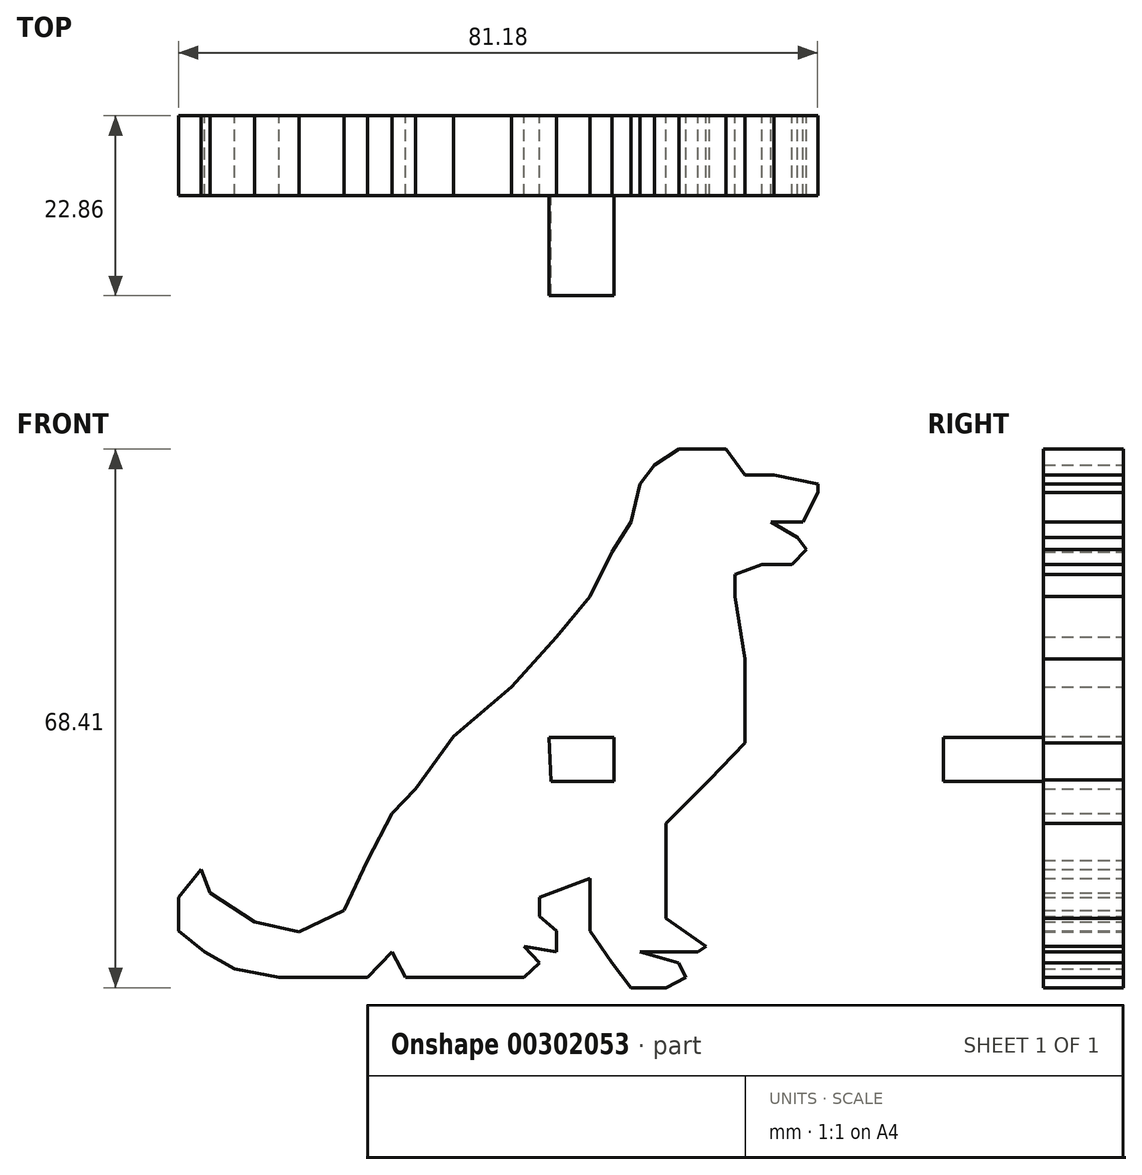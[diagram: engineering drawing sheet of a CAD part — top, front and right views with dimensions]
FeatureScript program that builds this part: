
annotation { "Feature Type Name" : "Feature", "Feature Type Description" : "" }
export const myFeature = defineFeature(function(context is Context, id is Id, definition is map)
    precondition{}
    {
        {
            var Q0;
            Q0=qCreatedBy(makeId("Front.planeOp"),FACE);
            var sketch = newSketch(context, id + "F0", { "sketchPlane" : qUnion([Q0])});
            skLineSegment(sketch, "E0", {"start": v(-46.88, 88.84) * mm, "end": v(-48.72, 86.43) * mm});
            skLineSegment(sketch, "E1", {"start": v(-48.72, 86.43) * mm, "end": v(-49.86, 81.6) * mm});
            skLineSegment(sketch, "E2", {"start": v(-49.86, 81.6) * mm, "end": v(-52.27, 77.77) * mm});
            skLineSegment(sketch, "E3", {"start": v(-52.27, 77.77) * mm, "end": v(-55.1, 72.1) * mm});
            skLineSegment(sketch, "E4", {"start": v(-55.1, 72.1) * mm, "end": v(-59.37, 66.99) * mm});
            skLineSegment(sketch, "E5", {"start": v(-59.37, 66.99) * mm, "end": v(-65.04, 60.6) * mm});
            skLineSegment(sketch, "E6", {"start": v(-65.04, 60.6) * mm, "end": v(-72.42, 54.35) * mm});
            skLineSegment(sketch, "E7", {"start": v(-72.42, 54.35) * mm, "end": v(-77.25, 47.68) * mm});
            skLineSegment(sketch, "E8", {"start": v(-77.25, 47.68) * mm, "end": v(-80.23, 44.56) * mm});
            skLineSegment(sketch, "E9", {"start": v(-80.23, 44.56) * mm, "end": v(-83.35, 38.6) * mm});
            skLineSegment(sketch, "E10", {"start": v(-83.35, 38.6) * mm, "end": v(-86.33, 32.21) * mm});
            skLineSegment(sketch, "E11", {"start": v(-86.33, 32.21) * mm, "end": v(-92, 29.52) * mm});
            skLineSegment(sketch, "E12", {"start": v(-92, 29.52) * mm, "end": v(-97.69, 30.8) * mm});
            skLineSegment(sketch, "E13", {"start": v(-97.69, 30.8) * mm, "end": v(-103.36, 34.48) * mm});
            skLineSegment(sketch, "E14", {"start": v(-103.36, 34.48) * mm, "end": v(-104.5, 37.47) * mm});
            skLineSegment(sketch, "E15", {"start": v(-104.5, 37.47) * mm, "end": v(-107.34, 33.92) * mm});
            skLineSegment(sketch, "E16", {"start": v(-107.34, 33.92) * mm, "end": v(-107.34, 29.66) * mm});
            skLineSegment(sketch, "E17", {"start": v(-107.34, 29.66) * mm, "end": v(-104.07, 26.96) * mm});
            skLineSegment(sketch, "E18", {"start": v(-104.07, 26.96) * mm, "end": v(-100.24, 24.83) * mm});
            skLineSegment(sketch, "E19", {"start": v(-100.24, 24.83) * mm, "end": v(-94.56, 23.7) * mm});
            skLineSegment(sketch, "E20", {"start": v(-94.56, 23.7) * mm, "end": v(-88.6, 23.7) * mm});
            skLineSegment(sketch, "E21", {"start": v(-88.6, 23.7) * mm, "end": v(-83.35, 23.7) * mm});
            skLineSegment(sketch, "E22", {"start": v(-83.35, 23.7) * mm, "end": v(-80.23, 26.96) * mm});
            skLineSegment(sketch, "E23", {"start": v(-80.23, 26.96) * mm, "end": v(-78.53, 23.7) * mm});
            skLineSegment(sketch, "E24", {"start": v(-78.53, 23.7) * mm, "end": v(-70.15, 23.7) * mm});
            skLineSegment(sketch, "E25", {"start": v(-70.15, 23.7) * mm, "end": v(-63.48, 23.7) * mm});
            skLineSegment(sketch, "E26", {"start": v(-63.48, 23.7) * mm, "end": v(-61.5, 25.54) * mm});
            skLineSegment(sketch, "E27", {"start": v(-61.5, 25.54) * mm, "end": v(-63.48, 27.68) * mm});
            skLineSegment(sketch, "E28", {"start": v(-63.48, 27.68) * mm, "end": v(-59.37, 26.96) * mm});
            skLineSegment(sketch, "E29", {"start": v(-59.37, 26.96) * mm, "end": v(-59.37, 29.66) * mm});
            skLineSegment(sketch, "E30", {"start": v(-59.37, 29.66) * mm, "end": v(-61.5, 31.5) * mm});
            skLineSegment(sketch, "E31", {"start": v(-61.5, 31.5) * mm, "end": v(-61.5, 33.92) * mm});
            skLineSegment(sketch, "E32", {"start": v(-61.5, 33.92) * mm, "end": v(-55.1, 36.33) * mm});
            skLineSegment(sketch, "E33", {"start": v(-55.1, 36.33) * mm, "end": v(-55.1, 29.66) * mm});
            skLineSegment(sketch, "E34", {"start": v(-55.1, 29.66) * mm, "end": v(-52.27, 25.54) * mm});
            skLineSegment(sketch, "E35", {"start": v(-52.27, 25.54) * mm, "end": v(-49.86, 22.42) * mm});
            skLineSegment(sketch, "E36", {"start": v(-49.86, 22.42) * mm, "end": v(-45.46, 22.42) * mm});
            skLineSegment(sketch, "E37", {"start": v(-45.46, 22.42) * mm, "end": v(-42.9, 23.7) * mm});
            skLineSegment(sketch, "E38", {"start": v(-42.9, 23.7) * mm, "end": v(-43.83, 25.54) * mm});
            skLineSegment(sketch, "E39", {"start": v(-43.83, 25.54) * mm, "end": v(-48.72, 26.96) * mm});
            skLineSegment(sketch, "E40", {"start": v(-48.72, 26.96) * mm, "end": v(-41.34, 26.96) * mm});
            skLineSegment(sketch, "E41", {"start": v(-41.34, 26.96) * mm, "end": v(-40.35, 27.68) * mm});
            skLineSegment(sketch, "E42", {"start": v(-40.35, 27.68) * mm, "end": v(-45.46, 31.22) * mm});
            skLineSegment(sketch, "E43", {"start": v(-45.46, 31.22) * mm, "end": v(-45.46, 36.33) * mm});
            skLineSegment(sketch, "E44", {"start": v(-45.46, 36.33) * mm, "end": v(-45.46, 43.28) * mm});
            skLineSegment(sketch, "E45", {"start": v(-45.46, 43.28) * mm, "end": v(-39.92, 48.82) * mm});
            skLineSegment(sketch, "E46", {"start": v(-39.92, 48.82) * mm, "end": v(-35.38, 53.5) * mm});
            skLineSegment(sketch, "E47", {"start": v(-35.38, 53.5) * mm, "end": v(-35.38, 58.61) * mm});
            skLineSegment(sketch, "E48", {"start": v(-35.38, 58.61) * mm, "end": v(-35.38, 64.15) * mm});
            skLineSegment(sketch, "E49", {"start": v(-35.38, 64.15) * mm, "end": v(-36.66, 72.1) * mm});
            skLineSegment(sketch, "E50", {"start": v(-36.66, 72.1) * mm, "end": v(-36.66, 74.93) * mm});
            skLineSegment(sketch, "E51", {"start": v(-36.66, 74.93) * mm, "end": v(-33.25, 76.21) * mm});
            skLineSegment(sketch, "E52", {"start": v(-33.25, 76.21) * mm, "end": v(-29.42, 76.21) * mm});
            skLineSegment(sketch, "E53", {"start": v(-29.42, 76.21) * mm, "end": v(-27.58, 78.06) * mm});
            skLineSegment(sketch, "E54", {"start": v(-27.58, 78.06) * mm, "end": v(-28.71, 79.62) * mm});
            skLineSegment(sketch, "E55", {"start": v(-28.71, 79.62) * mm, "end": v(-32.12, 81.6) * mm});
            skLineSegment(sketch, "E56", {"start": v(-32.12, 81.6) * mm, "end": v(-28, 81.6) * mm});
            skLineSegment(sketch, "E57", {"start": v(-28, 81.6) * mm, "end": v(-26.16, 85.3) * mm});
            skLineSegment(sketch, "E58", {"start": v(-26.16, 85.3) * mm, "end": v(-26.16, 86.43) * mm});
            skLineSegment(sketch, "E59", {"start": v(-26.16, 86.43) * mm, "end": v(-31.7, 87.56) * mm});
            skLineSegment(sketch, "E60", {"start": v(-31.7, 87.56) * mm, "end": v(-35.38, 87.56) * mm});
            skLineSegment(sketch, "E61", {"start": v(-35.38, 87.56) * mm, "end": v(-37.8, 90.83) * mm});
            skLineSegment(sketch, "E62", {"start": v(-37.8, 90.83) * mm, "end": v(-43.76, 90.83) * mm});
            skLineSegment(sketch, "E63", {"start": v(-43.76, 90.83) * mm, "end": v(-46.88, 88.84) * mm});
            skSolve(sketch);
        }
        {
            var Q0;
            Q0=makeQuery(id+"F0.imprint","IMPRINT",FACE,{"disambiguationData":[TD([[makeQuery(id+"F0.imprint","IMPRINT",EDGE,{"derivedFrom":sQuery(id+"F0.wireOp",EDGE,"E0")}),1.0]])]});
            extrude(context, id + "F1", {"entities" : qUnion([Q0]), "depth" : 10.16 * mm});
        }
        {
            var Q0;
            Q0=makeQuery(id+"F1.opExtrude","CAP_FACE",FACE,{"disambiguationData":[OSD([sQuery(id+"F0.wireOp",EDGE,"E0"),sQuery(id+"F0.wireOp",EDGE,"E1"),sQuery(id+"F0.wireOp",EDGE,"E2"),sQuery(id+"F0.wireOp",EDGE,"E3"),sQuery(id+"F0.wireOp",EDGE,"E4"),sQuery(id+"F0.wireOp",EDGE,"E5"),sQuery(id+"F0.wireOp",EDGE,"E6"),sQuery(id+"F0.wireOp",EDGE,"E7"),sQuery(id+"F0.wireOp",EDGE,"E8"),sQuery(id+"F0.wireOp",EDGE,"E9"),sQuery(id+"F0.wireOp",EDGE,"E10"),sQuery(id+"F0.wireOp",EDGE,"E11"),sQuery(id+"F0.wireOp",EDGE,"E12"),sQuery(id+"F0.wireOp",EDGE,"E13"),sQuery(id+"F0.wireOp",EDGE,"E14"),sQuery(id+"F0.wireOp",EDGE,"E15"),sQuery(id+"F0.wireOp",EDGE,"E16"),sQuery(id+"F0.wireOp",EDGE,"E17"),sQuery(id+"F0.wireOp",EDGE,"E18"),sQuery(id+"F0.wireOp",EDGE,"E19"),sQuery(id+"F0.wireOp",EDGE,"E20"),sQuery(id+"F0.wireOp",EDGE,"E21"),sQuery(id+"F0.wireOp",EDGE,"E22"),sQuery(id+"F0.wireOp",EDGE,"E23"),sQuery(id+"F0.wireOp",EDGE,"E24"),sQuery(id+"F0.wireOp",EDGE,"E25"),sQuery(id+"F0.wireOp",EDGE,"E26"),sQuery(id+"F0.wireOp",EDGE,"E27"),sQuery(id+"F0.wireOp",EDGE,"E28"),sQuery(id+"F0.wireOp",EDGE,"E29"),sQuery(id+"F0.wireOp",EDGE,"E30"),sQuery(id+"F0.wireOp",EDGE,"E31"),sQuery(id+"F0.wireOp",EDGE,"E32"),sQuery(id+"F0.wireOp",EDGE,"E33"),sQuery(id+"F0.wireOp",EDGE,"E34"),sQuery(id+"F0.wireOp",EDGE,"E35"),sQuery(id+"F0.wireOp",EDGE,"E36"),sQuery(id+"F0.wireOp",EDGE,"E37"),sQuery(id+"F0.wireOp",EDGE,"E38"),sQuery(id+"F0.wireOp",EDGE,"E39"),sQuery(id+"F0.wireOp",EDGE,"E40"),sQuery(id+"F0.wireOp",EDGE,"E41"),sQuery(id+"F0.wireOp",EDGE,"E42"),sQuery(id+"F0.wireOp",EDGE,"E43"),sQuery(id+"F0.wireOp",EDGE,"E44"),sQuery(id+"F0.wireOp",EDGE,"E45"),sQuery(id+"F0.wireOp",EDGE,"E46"),sQuery(id+"F0.wireOp",EDGE,"E47"),sQuery(id+"F0.wireOp",EDGE,"E48"),sQuery(id+"F0.wireOp",EDGE,"E49"),sQuery(id+"F0.wireOp",EDGE,"E50"),sQuery(id+"F0.wireOp",EDGE,"E51"),sQuery(id+"F0.wireOp",EDGE,"E52"),sQuery(id+"F0.wireOp",EDGE,"E53"),sQuery(id+"F0.wireOp",EDGE,"E54"),sQuery(id+"F0.wireOp",EDGE,"E55"),sQuery(id+"F0.wireOp",EDGE,"E56"),sQuery(id+"F0.wireOp",EDGE,"E57"),sQuery(id+"F0.wireOp",EDGE,"E58"),sQuery(id+"F0.wireOp",EDGE,"E59"),sQuery(id+"F0.wireOp",EDGE,"E60"),sQuery(id+"F0.wireOp",EDGE,"E61"),sQuery(id+"F0.wireOp",EDGE,"E62"),sQuery(id+"F0.wireOp",EDGE,"E63")])],"isStart":false});
            var sketch = newSketch(context, id + "F2", { "sketchPlane" : qUnion([Q0])});
            skLineSegment(sketch, "E64", {"start": v(-60.26, 54.2) * mm, "end": v(-52, 54.2) * mm});
            skLineSegment(sketch, "E65", {"start": v(-52, 54.2) * mm, "end": v(-52, 48.6) * mm});
            skLineSegment(sketch, "E66", {"start": v(-52, 48.6) * mm, "end": v(-60.02, 48.6) * mm});
            skLineSegment(sketch, "E67", {"start": v(-60.02, 48.6) * mm, "end": v(-60.26, 54.2) * mm});
            skSolve(sketch);
        }
        {
            var Q0;
            Q0 = qSketchRegion(id + "F2", true);
            extrude(context, id + "F3", {"entities" : qUnion([Q0]), "operationType" : NewBodyOperationType.ADD, "depth" : 12.7 * mm});
        }
    });
